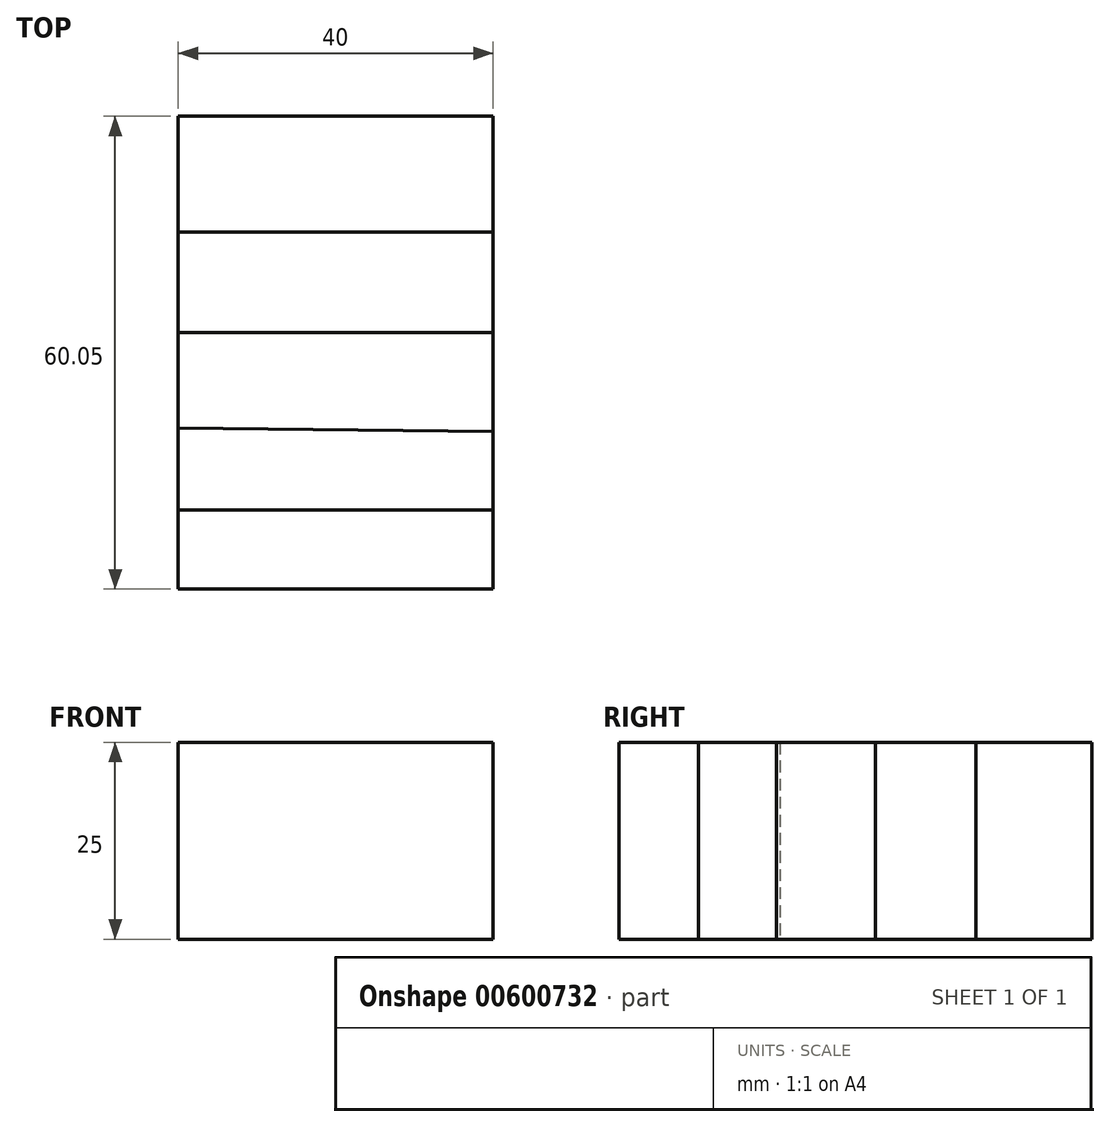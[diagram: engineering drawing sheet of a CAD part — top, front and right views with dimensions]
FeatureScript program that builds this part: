
annotation { "Feature Type Name" : "Feature", "Feature Type Description" : "" }
export const myFeature = defineFeature(function(context is Context, id is Id, definition is map)
    precondition{}
    {
        {
            var Q0;
            Q0=qCreatedBy(makeId("Top.planeOp"),FACE);
            var sketch = newSketch(context, id + "F0", { "sketchPlane" : qUnion([Q0])});
            skLineSegment(sketch, "E0", {"start": v(0, 0) * mm, "end": v(0, -20) * mm, "construction": true});
            skLineSegment(sketch, "E1", {"start": v(0, -20) * mm, "end": v(-20, -20) * mm});
            skLineSegment(sketch, "E2", {"start": v(-20, -20) * mm, "end": v(-20, -9.95) * mm});
            skLineSegment(sketch, "E3", {"start": v(-20, -9.95) * mm, "end": v(-20, 0.45) * mm});
            skLineSegment(sketch, "E4", {"start": v(-20, 0.45) * mm, "end": v(-20, 12.55) * mm});
            skLineSegment(sketch, "E5", {"start": v(-20, 12.55) * mm, "end": v(-20, 25.35) * mm});
            skLineSegment(sketch, "E6", {"start": v(-20, 25.35) * mm, "end": v(-20, 40.05) * mm});
            skLineSegment(sketch, "E7", {"start": v(-20, 40.05) * mm, "end": v(20, 40.05) * mm});
            skLineSegment(sketch, "E8", {"start": v(20, 40.05) * mm, "end": v(20, -20) * mm});
            skLineSegment(sketch, "E9", {"start": v(20, -20) * mm, "end": v(0, -20) * mm});
            skLineSegment(sketch, "E10", {"start": v(-20, 25.35) * mm, "end": v(20, 25.35) * mm});
            skLineSegment(sketch, "E11", {"start": v(-20, 12.55) * mm, "end": v(20, 12.55) * mm});
            skLineSegment(sketch, "E12", {"start": v(-20, 0.45) * mm, "end": v(20, 0) * mm});
            skLineSegment(sketch, "E13", {"start": v(-20, -9.95) * mm, "end": v(20, -9.95) * mm});
            skSolve(sketch);
        }
        {
            var Q0;
            Q0=makeQuery(id+"F0.imprint","IMPRINT",FACE,{"disambiguationData":[TD([[makeQuery(id+"F0.imprint","IMPRINT",EDGE,{"derivedFrom":sQuery(id+"F0.wireOp",EDGE,"E6")}),-1.0]])]});
            extrude(context, id + "F1", {"entities" : qUnion([Q0]), "depth" : 25 * mm, "offsetDistance" : 25 * mm});
        }
        {
            var Q0;
            Q0=makeQuery(id+"F0.imprint","IMPRINT",FACE,{"disambiguationData":[TD([[makeQuery(id+"F0.imprint","IMPRINT",EDGE,{"derivedFrom":sQuery(id+"F0.wireOp",EDGE,"E5")}),-1.0]])]});
            extrude(context, id + "F2", {"entities" : qUnion([Q0]), "depth" : 25 * mm, "offsetDistance" : 25 * mm});
        }
        {
            var Q0;
            Q0=makeQuery(id+"F0.imprint","IMPRINT",FACE,{"disambiguationData":[TD([[makeQuery(id+"F0.imprint","IMPRINT",EDGE,{"derivedFrom":sQuery(id+"F0.wireOp",EDGE,"E4")}),-1.0]])]});
            extrude(context, id + "F3", {"entities" : qUnion([Q0]), "depth" : 25 * mm, "offsetDistance" : 25 * mm});
        }
        {
            var Q0;
            Q0=makeQuery(id+"F0.imprint","IMPRINT",FACE,{"disambiguationData":[TD([[makeQuery(id+"F0.imprint","IMPRINT",EDGE,{"derivedFrom":sQuery(id+"F0.wireOp",EDGE,"E3")}),-1.0]])]});
            extrude(context, id + "F4", {"entities" : qUnion([Q0]), "depth" : 25 * mm, "offsetDistance" : 25 * mm});
        }
        {
            var Q0;
            Q0=makeQuery(id+"F0.imprint","IMPRINT",FACE,{"disambiguationData":[TD([[makeQuery(id+"F0.imprint","IMPRINT",EDGE,{"derivedFrom":sQuery(id+"F0.wireOp",EDGE,"E1")}),-1.0]])]});
            extrude(context, id + "F5", {"entities" : qUnion([Q0]), "depth" : 25 * mm, "offsetDistance" : 25 * mm});
        }
    });
